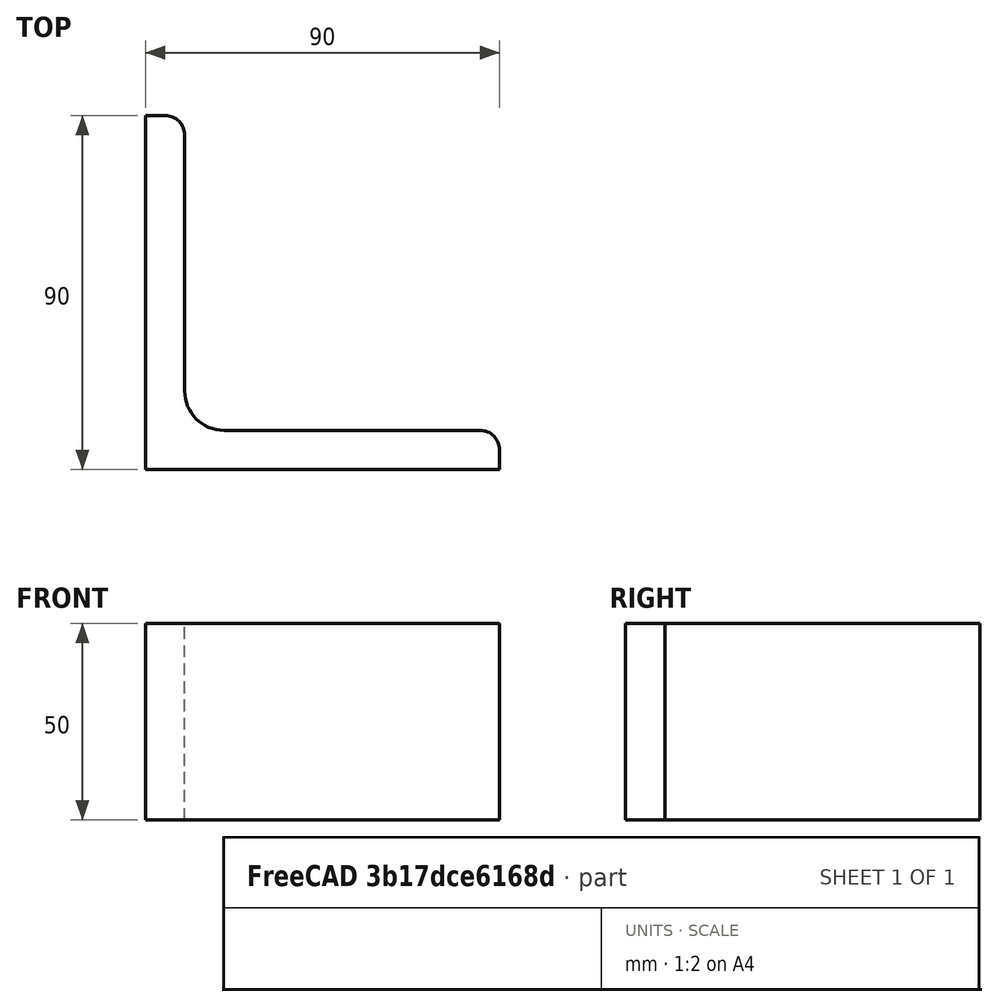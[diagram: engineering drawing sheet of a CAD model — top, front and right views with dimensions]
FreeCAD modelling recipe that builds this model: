
FCSTD DOCUMENT  (FreeCAD 0.15R4671 (Git))
Label: Angle Bar L90x90x10 EN10056 S235JR
License: All rights reserved
LicenseURL: http://en.wikipedia.org/wiki/All_rights_reserved
objects: Sketcher::SketchObject×1, Part::Extrusion×1
note: 2 computed .brp shape members not serialized (recipe doc carries the construction recipe); baked Part::Feature solids carry a one-line shape summary decoded from their .brp

FEATURE [Sketcher::SketchObject] Sketch
  sketch-geometry (9):
    g0: LineSegment StartX=0 StartY=0 StartZ=0 EndX=90 EndY=0 EndZ=0
    g1: LineSegment StartX=90 StartY=0 StartZ=0 EndX=90 EndY=5 EndZ=0
    g2: LineSegment StartX=85 StartY=10 StartZ=0 EndX=20 EndY=10 EndZ=0
    g3: LineSegment StartX=0 StartY=0 StartZ=0 EndX=0 EndY=90 EndZ=0
    g4: LineSegment StartX=0 StartY=90 StartZ=0 EndX=5 EndY=90 EndZ=0
    g5: LineSegment StartX=10 StartY=85 StartZ=0 EndX=10 EndY=20 EndZ=0
    g6: ArcOfCircle CenterX=20 CenterY=20 CenterZ=0 NormalX=0 NormalY=0 NormalZ=1 Radius=10 StartAngle=3.14159 EndAngle=4.71239
    g7: ArcOfCircle CenterX=5 CenterY=85 CenterZ=0 NormalX=0 NormalY=0 NormalZ=1 Radius=5 StartAngle=0 EndAngle=1.5708
    g8: ArcOfCircle CenterX=85 CenterY=5 CenterZ=0 NormalX=0 NormalY=0 NormalZ=1 Radius=5 StartAngle=0 EndAngle=1.5708
  constraints (23):
    c: Coincident(g0,g-1)
    c: Horizontal(g0)
    c: Coincident(g1,g0)
    c: Vertical(g1)
    c: Horizontal(g2)
    c: Coincident(g3,g-1)
    c: Vertical(g3)
    c: Coincident(g4,g3)
    c: Horizontal(g4)
    c: Vertical(g5)
    c: Tangent(g5,g6) = -1.5708
    c: Tangent(g2,g6) = 1.5708
    c: Tangent(g4,g7) = 1.5708
    c: Tangent(g5,g7) = 1.5708
    c: Tangent(g2,g8) = -1.5708
    c: Tangent(g1,g8) = -1.5708
    c: DistanceX(g0) = 90
    c: DistanceY(g3) = 90
    c: DistanceY(g0,g2) = 10
    c: DistanceX(g3,g5) = 10
    c: Radius(g6) = 10
    c: Radius(g8) = 5
    c: Radius(g7) = 5
FEATURE [Part::Extrusion] Extrude  label="Angle Bar L90x90x10 EN10056 S235JR"
  Base = -> Sketch
  Dir = (0,0,50)
  Solid = true
